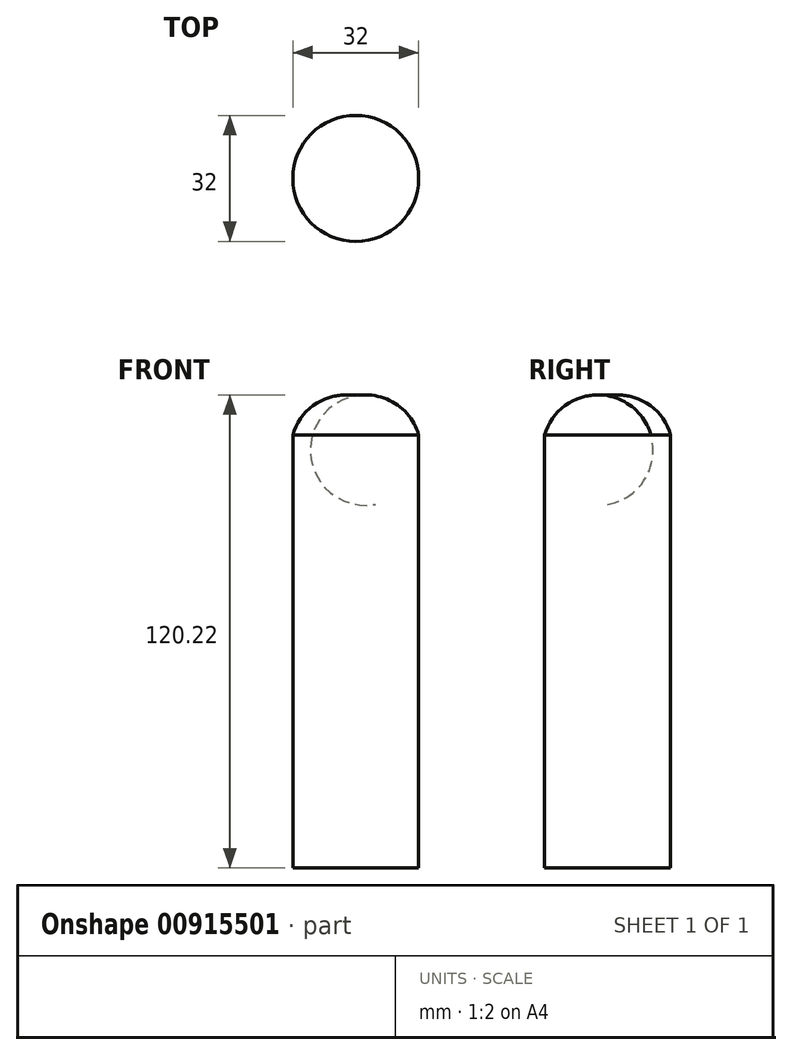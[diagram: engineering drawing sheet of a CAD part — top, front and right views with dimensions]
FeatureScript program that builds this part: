
annotation { "Feature Type Name" : "Feature", "Feature Type Description" : "" }
export const myFeature = defineFeature(function(context is Context, id is Id, definition is map)
    precondition{}
    {
        {
            var Q0;
            Q0=qCreatedBy(makeId("Front.planeOp"),FACE);
            var sketch = newSketch(context, id + "F0", { "sketchPlane" : qUnion([Q0])});
            skLineSegment(sketch, "E0", {"start": v(0, 0) * mm, "end": v(-16, 0) * mm});
            skLineSegment(sketch, "E1", {"start": v(-16, 0) * mm, "end": v(-16, 110) * mm});
            skArc(sketch, "E2", {"start": v(-16, 110) * mm, "mid": v(-9.93, 118.1) * mm, "end": v(0, 120) * mm});
            skLineSegment(sketch, "E3", {"start": v(0, 120) * mm, "end": v(0, 0) * mm});
            skSolve(sketch);
        }
        {
            var Q0;
            Q0=makeQuery(id+"F0.imprint","IMPRINT",FACE,{"disambiguationData":[TD([[makeQuery(id+"F0.imprint","IMPRINT",EDGE,{"derivedFrom":sQuery(id+"F0.wireOp",EDGE,"E0")}),-1.0]])]});
            var Q1;
            Q1=sQuery(id+"F0.wireOp",EDGE,"E3");
            revolve(context, id + "F1", {"surfaceOperationType" : NewSurfaceOperationType.NEW, "entities" : qUnion([Q0]), "axis" : qUnion([Q1]), "revolveType" : RevolveType.FULL});
        }
    });
